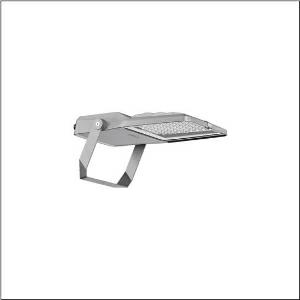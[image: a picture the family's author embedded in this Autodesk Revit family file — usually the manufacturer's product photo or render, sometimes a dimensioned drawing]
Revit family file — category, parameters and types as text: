
# Revit family: floodlight_fl_21_iq_mini___pl33t_5xa7771d4f1a_3e9c
name_source: partatom
category: Lighting Fixtures
units: mm (PartAtom-declared; Revit-internal decimal feet)

## family parameters
Cut with Voids When Loaded = No
Host = Face
Light Source = No
Part Type = Normal
Room Calculation Point = No
Round Connector Dimension = Use Diameter
Shared = No

## types (1)
- --- (1 x LED, 18390 lm, 143 W, 4000K)
    Apparent Load = 143 VA
    CIE Flux Codes = 26 75 99 100 100
    Color Rendering = 70
    Color Temperature = 4000K
    Default Elevation = 1800 mm
    Description = Floodlight FL 21 iQ mini, floodlight, primary light control with lens, of PMMA, primary optical cover: protective disc, of toughened safety glass, transparent, light distribution: PL33T, light emission: direct distribution, installation type: surface-mounted, LED, High Power LED, rated luminous flux: 18.390lm, luminous efficacy: 129lm/W, light colour: 740, colour temperature: 4000K, control gear: iQ Comfort/DALI, control: Auto-Match, Temp-Guard, Lumen-Switch, Night-Set, Smart-Wire, Light-Fading, Desk-Remote (wireless, voltage-free reading and setting of iQ features in the workshop via application-optimized NFC function/RFID function), optimised constant luminous flux control (CLO 2.0), with terminal, 6-pole, mains connection: 220..240V, AC, 50/60Hz, start of lifetime: 143W, end of service life: 152W, reduction: 61W, luminaire housing, of diecast aluminium, powder-coated, Siteco® metallic grey (DB 702S), corrosivity category C5 mid according to DIN EN ISO 12944, suitable for swimming pools, chlorine-resistant, sealing non-destructively replaceable, mounting bracket, of steel, galvanised, powder-coated, Siteco® metallic grey (DB 702S), protection rating (complete): IP66, insulation class (complete): insulation class II (safety insulation), certification: CE, ENEC, VDE, protection symbol: D, impact resistance: IK08, permissible operating ambient temperature: -40..+40°C, permissible operating ambient temperature for outdoor applications: -40..+50°C, standard: DIN EN 12944, LABS conformity tested according to VDMA 24364:2018-05, packaging unit: 1 piece

Light Distribution: PL33T
    Height = 70 mm
    Lamp = 1 x LED
    Lamp Light Flux = 18390 lm
    Lamp Power = 143 W
    Lamp count = 1
    Length = 485 mm
    Luminous efficacy = 129 lm/W
    Manufacturer = Siteco
    ModVariant = No
    Model = 5XA7771D4F1A
    Number of Poles = 1
    OnlyDefault = Yes
    Power Factor = 1
    Product Name = Floodlight FL 21 iQ mini | PL33T
    Product group = floodlight | pylon annexe
    ProductGroupID = 6200
    Protection Class = Protection class II
    Protection Degree = IP 66
    RLX_Detail_Level = 1
    RLX_Emergency_Light_Flux = 0 lm
    RLX_Emergency_Type = 0
    RLX_Emergency_Type_DB = No
    RlxData = <blob elided: 96629 chars, md5=1ae46913>
    Socket = socket
    Standby Power = 0 W
    System Light Flux = 18390 lm
    System Power = 143 W
    Type Comments = factory setting: luminous flux: 100 % | dim-lin: 254 | 730 mA
    Type Image = l_1006845.jpg
    URL = http://relux.com
    VarID = @adj_149160
    Voltage = 0 V
    Weight = 0.00 kg
    Width = 337 mm

## geometry (parser evidence)
native form markers: Blend x4, Sweep x11
no freeform markers — native parametric forms only
